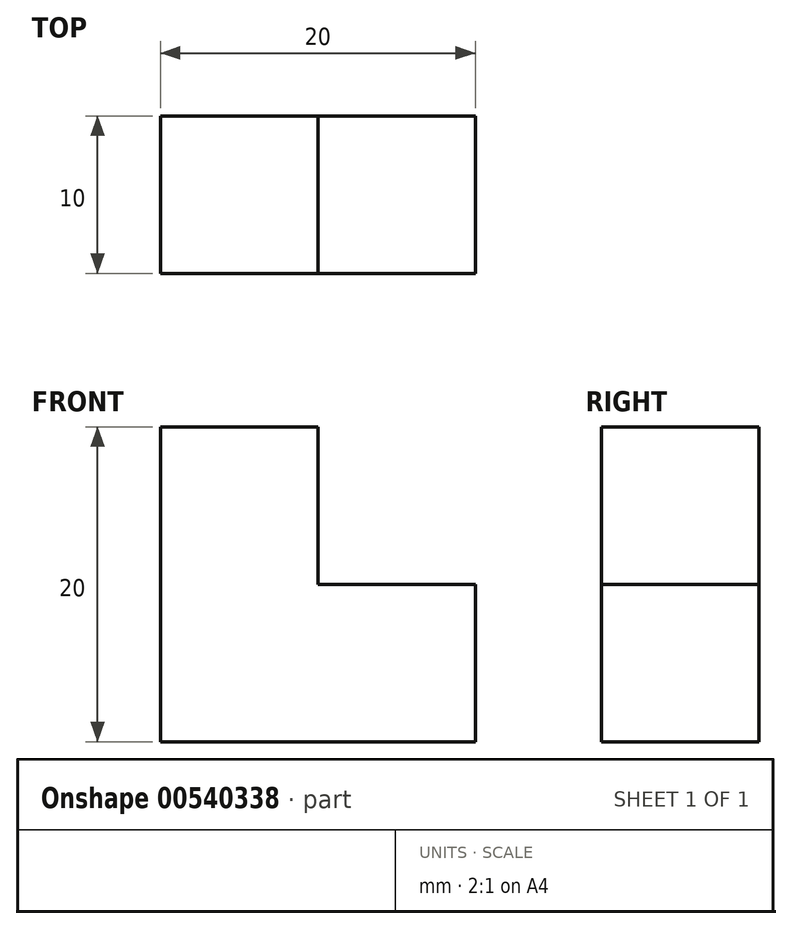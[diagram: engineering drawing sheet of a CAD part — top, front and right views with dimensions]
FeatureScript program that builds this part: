
annotation { "Feature Type Name" : "Feature", "Feature Type Description" : "" }
export const myFeature = defineFeature(function(context is Context, id is Id, definition is map)
    precondition{}
    {
        {
            var Q0;
            Q0=qCreatedBy(makeId("Front.planeOp"),FACE);
            var sketch = newSketch(context, id + "F0", { "sketchPlane" : qUnion([Q0])});
            skLineSegment(sketch, "E0", {"start": v(0, 0) * mm, "end": v(20, 0) * mm});
            skLineSegment(sketch, "E1", {"start": v(20, 0) * mm, "end": v(20, 10) * mm});
            skLineSegment(sketch, "E2", {"start": v(20, 10) * mm, "end": v(10, 10) * mm});
            skLineSegment(sketch, "E3", {"start": v(10, 10) * mm, "end": v(10, 20) * mm});
            skLineSegment(sketch, "E4", {"start": v(10, 20) * mm, "end": v(0, 20) * mm});
            skLineSegment(sketch, "E5", {"start": v(0, 20) * mm, "end": v(0, 0) * mm});
            skSolve(sketch);
        }
        {
            var Q0;
            Q0=makeQuery(id+"F0.imprint","IMPRINT",FACE,{"disambiguationData":[TD([[makeQuery(id+"F0.imprint","IMPRINT",EDGE,{"derivedFrom":sQuery(id+"F0.wireOp",EDGE,"E0")}),1.0]])]});
            extrude(context, id + "F1", {"entities" : qUnion([Q0]), "depth" : 10 * mm, "offsetDistance" : 25 * mm});
        }
    });
